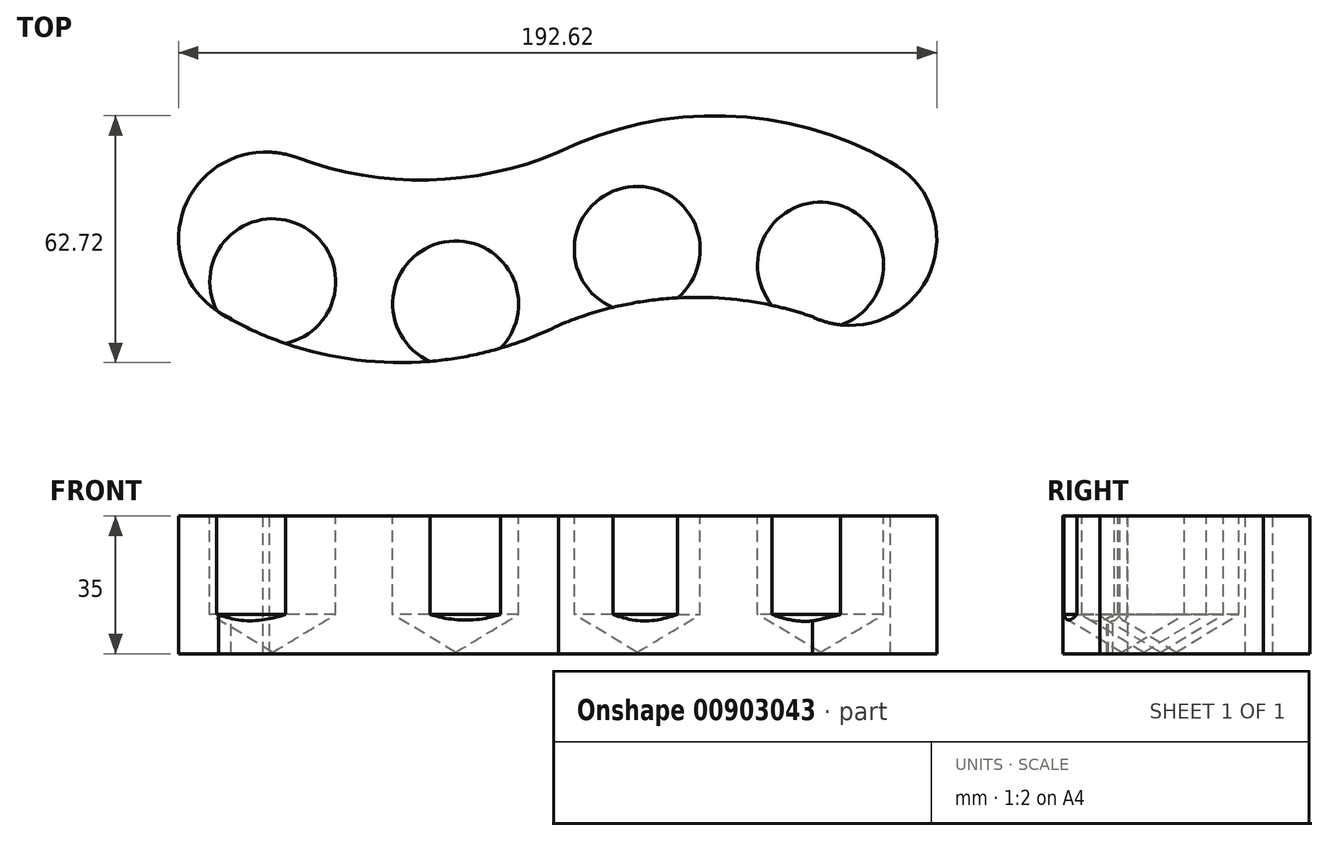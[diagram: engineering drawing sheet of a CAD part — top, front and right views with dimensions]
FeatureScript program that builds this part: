
annotation { "Feature Type Name" : "Feature", "Feature Type Description" : "" }
export const myFeature = defineFeature(function(context is Context, id is Id, definition is map)
    precondition{}
    {
        {
            var Q0;
            Q0=qCreatedBy(makeId("Front.planeOp"),FACE);
            var sketch = newSketch(context, id + "F0", { "sketchPlane" : qUnion([Q0])});
            skLineSegment(sketch, "E0.bottom", {"start": v(-96.5, 35) * mm, "end": v(96.5, 35) * mm});
            skLineSegment(sketch, "E0.top", {"start": v(-96.5, 0) * mm, "end": v(96.5, 0) * mm});
            skLineSegment(sketch, "E0.left", {"start": v(-96.5, 35) * mm, "end": v(-96.5, 0) * mm});
            skLineSegment(sketch, "E0.right", {"start": v(96.5, 35) * mm, "end": v(96.5, 0) * mm});
            skPoint(sketch, "E1", {"position": v(0, 0) * mm});
            skSolve(sketch);
        }
        {
            var Q0;
            Q0=makeQuery(id+"F0.imprint","IMPRINT",FACE,{"disambiguationData":[TD([[makeQuery(id+"F0.imprint","IMPRINT",EDGE,{"derivedFrom":sQuery(id+"F0.wireOp",EDGE,"E0.bottom")}),-1.0]])]});
            extrude(context, id + "F1", {"entities" : qUnion([Q0]), "depth" : 44 * mm, "offsetDistance" : 25 * mm});
        }
        {
            var Q0;
            Q0=makeQuery(id+"F1.opExtrude","SWEPT_FACE",FACE,{"disambiguationData":[OSD([sQuery(id+"F0.wireOp",EDGE,"E0.bottom")])]});
            var sketch = newSketch(context, id + "F2", { "sketchPlane" : qUnion([Q0])});
            skCircle(sketch, "E2", {"center": v(-74.5, -22) * mm, "radius": 22 * mm});
            skCircle(sketch, "E3", {"center": v(74.5, -22) * mm, "radius": 22 * mm});
            skPoint(sketch, "E4", {"position": v(-75.05, 0) * mm});
            skPoint(sketch, "E5", {"position": v(-73.9, -44) * mm});
            skLineSegment(sketch, "E6", {"start": v(-75.05, 0) * mm, "end": v(-96.5, 0) * mm});
            skLineSegment(sketch, "E7", {"start": v(-96.5, 0) * mm, "end": v(-96.5, -22) * mm});
            skLineSegment(sketch, "E8", {"start": v(-96.5, -22) * mm, "end": v(-96.5, -44) * mm});
            skLineSegment(sketch, "E9", {"start": v(-96.5, -44) * mm, "end": v(-73.9, -44) * mm});
            skLineSegment(sketch, "E10", {"start": v(96.5, -22) * mm, "end": v(96.5, 0) * mm});
            skPoint(sketch, "E10.startSnap0", {"position": v(96.5, -22) * mm});
            skLineSegment(sketch, "E11", {"start": v(96.5, 0) * mm, "end": v(75.19, 0) * mm});
            skLineSegment(sketch, "E12", {"start": v(96.5, -22) * mm, "end": v(96.5, -44) * mm});
            skLineSegment(sketch, "E13", {"start": v(96.5, -44) * mm, "end": v(74.92, -44) * mm});
            skSolve(sketch);
        }
        {
            var Q0;
            {var subQ0=sQuery(id+"F2.wireOp",EDGE,"E6");Q0=makeQuery(id+"F2.imprint","IMPRINT",FACE,{"disambiguationData":[TD([[makeQuery(id+"F2.imprint","IMPRINT",EDGE,{"derivedFrom":subQ0}),-1.0]])]});}
            var Q1;
            {var subQ0=sQuery(id+"F2.wireOp",EDGE,"E8");Q1=makeQuery(id+"F2.imprint","IMPRINT",FACE,{"disambiguationData":[TD([[makeQuery(id+"F2.imprint","IMPRINT",EDGE,{"derivedFrom":subQ0}),-1.0]])]});}
            var Q2;
            {var subQ0=sQuery(id+"F2.wireOp",EDGE,"E10");Q2=makeQuery(id+"F2.imprint","IMPRINT",FACE,{"disambiguationData":[TD([[makeQuery(id+"F2.imprint","IMPRINT",EDGE,{"derivedFrom":subQ0}),1.0]])]});}
            var Q3;
            {var subQ0=sQuery(id+"F2.wireOp",EDGE,"2GBzTM6C-MvFQ-nlD2-Bbiq-WhvATEVppX7r");Q3=makeQuery(id+"F2.imprint","IMPRINT",FACE,{"disambiguationData":[TD([[makeQuery(id+"F2.imprint","IMPRINT",EDGE,{"derivedFrom":subQ0}),-1.0]])]});}
            var Q4;
            {var subQ0=sQuery(id+"F2.wireOp",EDGE,"E12");Q4=makeQuery(id+"F2.imprint","IMPRINT",FACE,{"disambiguationData":[TD([[makeQuery(id+"F2.imprint","IMPRINT",EDGE,{"derivedFrom":subQ0}),1.0]])]});}
            extrude(context, id + "F3", {"entities" : qUnion([Q0, Q1, Q2, Q3, Q4]), "operationType" : NewBodyOperationType.REMOVE, "endBound" : BoundingType.THROUGH_ALL, "oppositeDirection" : true, "depth" : 25 * mm, "offsetDistance" : 25 * mm});
        }
        {
            var Q0;
            Q0=makeQuery(id+"F1.opExtrude","SWEPT_FACE",FACE,{"disambiguationData":[OSD([sQuery(id+"F0.wireOp",EDGE,"E0.bottom")])]});
            var sketch = newSketch(context, id + "F4", { "sketchPlane" : qUnion([Q0])});
            skCircle(sketch, "E14", {"center": v(-74.11, -22) * mm, "radius": 22 * mm});
            skArc(sketch, "E15", {"start": v(-66.36, -1.4) * mm, "mid": v(-33.05, -7.04) * mm, "end": v(0, 0) * mm});
            skCircle(sketch, "E16", {"center": v(74.11, -22) * mm, "radius": 22 * mm});
            skArc(sketch, "E17", {"start": v(68.47, -43.26) * mm, "mid": v(34.16, -36.86) * mm, "end": v(0, -44) * mm});
            skLineSegment(sketch, "E18", {"start": v(-75.05, 0) * mm, "end": v(0, 0) * mm, "construction": true});
            skLineSegment(sketch, "E19", {"start": v(74.92, -44) * mm, "end": v(0, -44) * mm, "construction": true});
            skSolve(sketch);
        }
        {
            var Q0;
            {var subQ0=sQuery(id+"F4.wireOp",EDGE,"E15");Q0=makeQuery(id+"F4.imprint","IMPRINT",FACE,{"disambiguationData":[TD([[makeQuery(id+"F4.imprint","IMPRINT",EDGE,{"derivedFrom":subQ0}),1.0]])]});}
            var Q1;
            {var subQ0=sQuery(id+"F4.wireOp",EDGE,"E17");var subQ5=sQuery(id+"F4.wireOp",EDGE,"E16");var subQ7=makeQuery(id+"F4.imprint","INTERSECT",VERTEX,{"disambiguationData":[OD(0.0)],"derivedFrom":[subQ5,subQ0]});Q1=makeQuery(id+"F4.imprint","IMPRINT",FACE,{"disambiguationData":[TD([[makeQuery(id+"F4.imprint","IMPRINT",EDGE,{"disambiguationData":[TD([[subQ7,1.0]])],"derivedFrom":subQ5}),-1.0]])]});}
            extrude(context, id + "F5", {"entities" : qUnion([Q0, Q1]), "operationType" : NewBodyOperationType.REMOVE, "endBound" : BoundingType.THROUGH_ALL, "oppositeDirection" : true, "depth" : 25 * mm, "offsetDistance" : 25 * mm});
        }
        {
            var Q0;
            Q0=makeQuery(id+"F1.opExtrude","SWEPT_FACE",FACE,{"disambiguationData":[OSD([sQuery(id+"F0.wireOp",EDGE,"E0.bottom")])]});
            var sketch = newSketch(context, id + "F6", { "sketchPlane" : qUnion([Q0])});
            skArc(sketch, "E20", {"start": v(86.09, -3.53) * mm, "mid": v(43.5, 9.2) * mm, "end": v(0, 0) * mm});
            skCircle(sketch, "E21", {"center": v(-74.11, -22) * mm, "radius": 22 * mm});
            skLineSegment(sketch, "E22", {"start": v(0, -44) * mm, "end": v(-71.01, -43.77) * mm});
            skCircle(sketch, "E23", {"center": v(74.11, -22) * mm, "radius": 22 * mm});
            skLineSegment(sketch, "E24", {"start": v(0, 0) * mm, "end": v(74.85, 0) * mm});
            skSolve(sketch);
        }
        {
            var Q0;
            {var subQ0=sQuery(id+"F6.wireOp",EDGE,"E24");var subQ3=sQuery(id+"F6.wireOp",EDGE,"E23");var subQ4=makeQuery(id+"F6.imprint","INTERSECT",VERTEX,{"disambiguationData":[OD(0.0)],"derivedFrom":[subQ3,subQ0]});Q0=makeQuery(id+"F6.imprint","IMPRINT",FACE,{"disambiguationData":[TD([[makeQuery(id+"F6.imprint","IMPRINT",EDGE,{"disambiguationData":[TD([[subQ4,-1.0]])],"derivedFrom":subQ3}),-1.0]])]});}
            var Q1;
            {var subQ0=sQuery(id+"F0.wireOp",EDGE,"E0.bottom");var subQ1=sQuery(id+"F0.wireOp",EDGE,"E0.top");Q1=makeQuery(id+"F5.boolean.opBoolean","SPLIT",FACE,{"disambiguationData":[TD([makeQuery(id+"F5.opExtrude","SWEPT_FACE",FACE,{"disambiguationData":[OSD([sQuery(id+"F4.wireOp",EDGE,"E15")])]})])],"derivedFrom":makeQuery(id+"F1.opExtrude","CAP_FACE",FACE,{"disambiguationData":[OSD([subQ0,subQ1,sQuery(id+"F0.wireOp",EDGE,"E0.left"),sQuery(id+"F0.wireOp",EDGE,"E0.right")])],"isStart":true})});}
            extrude(context, id + "F7", {"entities" : qUnion([Q0]), "operationType" : NewBodyOperationType.ADD, "oppositeDirection" : true, "depth" : 35 * mm, "endBoundEntityFace" : qUnion([Q1]), "offsetDistance" : 25 * mm});
        }
        {
            var Q0;
            Q0=makeQuery(id+"F7.boolean.opBoolean","MERGE",FACE,{"derivedFrom":[makeQuery(id+"F1.opExtrude","SWEPT_FACE",FACE,{"disambiguationData":[OSD([sQuery(id+"F0.wireOp",EDGE,"E0.bottom")])]}),makeQuery(id+"F7.opExtrude","CAP_FACE",FACE,{"disambiguationData":[OSD([sQuery(id+"F4.wireOp",EDGE,"E16"),sQuery(id+"F6.wireOp",EDGE,"E20"),sQuery(id+"F6.wireOp",EDGE,"E23"),sQuery(id+"F6.wireOp",EDGE,"E24")])],"isStart":true})]});
            var sketch = newSketch(context, id + "F8", { "sketchPlane" : qUnion([Q0])});
            skCircle(sketch, "E25", {"center": v(-75.13, -21.75) * mm, "radius": 22 * mm});
            skArc(sketch, "E26", {"start": v(-86.37, -40.66) * mm, "mid": v(-43.61, -53.38) * mm, "end": v(0, -44) * mm});
            skSolve(sketch);
        }
        {
            var Q0;
            {var subQ0=sQuery(id+"F8.wireOp",EDGE,"E26");Q0=makeQuery(id+"F8.imprint","IMPRINT",FACE,{"disambiguationData":[TD([[makeQuery(id+"F8.imprint","IMPRINT",EDGE,{"derivedFrom":subQ0}),1.0]])]});}
            extrude(context, id + "F9", {"entities" : qUnion([Q0]), "operationType" : NewBodyOperationType.ADD, "oppositeDirection" : true, "depth" : 35 * mm, "offsetDistance" : 25 * mm});
        }
        {
            var Q0;
            {var subQ0=sQuery(id+"F0.wireOp",EDGE,"E0.bottom");Q0=makeQuery(id+"F9.boolean.opBoolean","MERGE",FACE,{"derivedFrom":[makeQuery(id+"F7.boolean.opBoolean","MERGE",FACE,{"derivedFrom":[makeQuery(id+"F1.opExtrude","SWEPT_FACE",FACE,{"disambiguationData":[OSD([subQ0])]}),makeQuery(id+"F7.opExtrude","CAP_FACE",FACE,{"disambiguationData":[OSD([sQuery(id+"F4.wireOp",EDGE,"E16"),sQuery(id+"F6.wireOp",EDGE,"E20"),sQuery(id+"F6.wireOp",EDGE,"E23"),sQuery(id+"F6.wireOp",EDGE,"E24")])],"isStart":true})]}),makeQuery(id+"F9.opExtrude","CAP_FACE",FACE,{"disambiguationData":[OSD([subQ0,sQuery(id+"F2.wireOp",EDGE,"E2"),sQuery(id+"F8.wireOp",EDGE,"E25"),sQuery(id+"F8.wireOp",EDGE,"E26")])],"isStart":true})]});}
            var sketch = newSketch(context, id + "F10", { "sketchPlane" : qUnion([Q0])});
            skCircle(sketch, "E27", {"center": v(-72.58, -32.9) * mm, "radius": 15 * mm, "construction": true});
            skCircle(sketch, "E28", {"center": v(-26.1, -38.55) * mm, "radius": 15 * mm, "construction": true});
            skCircle(sketch, "E29", {"center": v(20.02, -24.68) * mm, "radius": 15 * mm, "construction": true});
            skCircle(sketch, "E30", {"center": v(66.6, -28.69) * mm, "radius": 15 * mm, "construction": true});
            skSolve(sketch);
        }
        {
            var Q0;
            Q0=sQuery(id+"F10.wireOp",VERTEX,"E27.center");
            var Q1;
            Q1=sQuery(id+"F10.wireOp",VERTEX,"E28.center");
            var Q2;
            Q2=sQuery(id+"F10.wireOp",VERTEX,"E29.center");
            var Q3;
            Q3=sQuery(id+"F10.wireOp",VERTEX,"E30.center");
            var Q4;
            Q4=makeQuery(id+"F1.opExtrude","SWEPT_BODY",BODY,{"disambiguationData":[OSD([sQuery(id+"F0.wireOp",EDGE,"E0.bottom"),sQuery(id+"F0.wireOp",EDGE,"E0.top"),sQuery(id+"F0.wireOp",EDGE,"E0.left"),sQuery(id+"F0.wireOp",EDGE,"E0.right")])]});
            hole(context, id + "F11", {"style" : HoleStyle.SIMPLE, "endStyle" : HoleEndStyle.BLIND, "holeDiameter" : 32 * mm, "majorDiameter" : 20 * mm, "holeDepth" : 25 * mm, "isTappedThrough" : true, "tappedDepth" : 3.5 * mm, "tapClearance" : 3, "locations" : qUnion([Q0, Q1, Q2, Q3]), "scope" : qUnion([Q4])});
        }
    });
